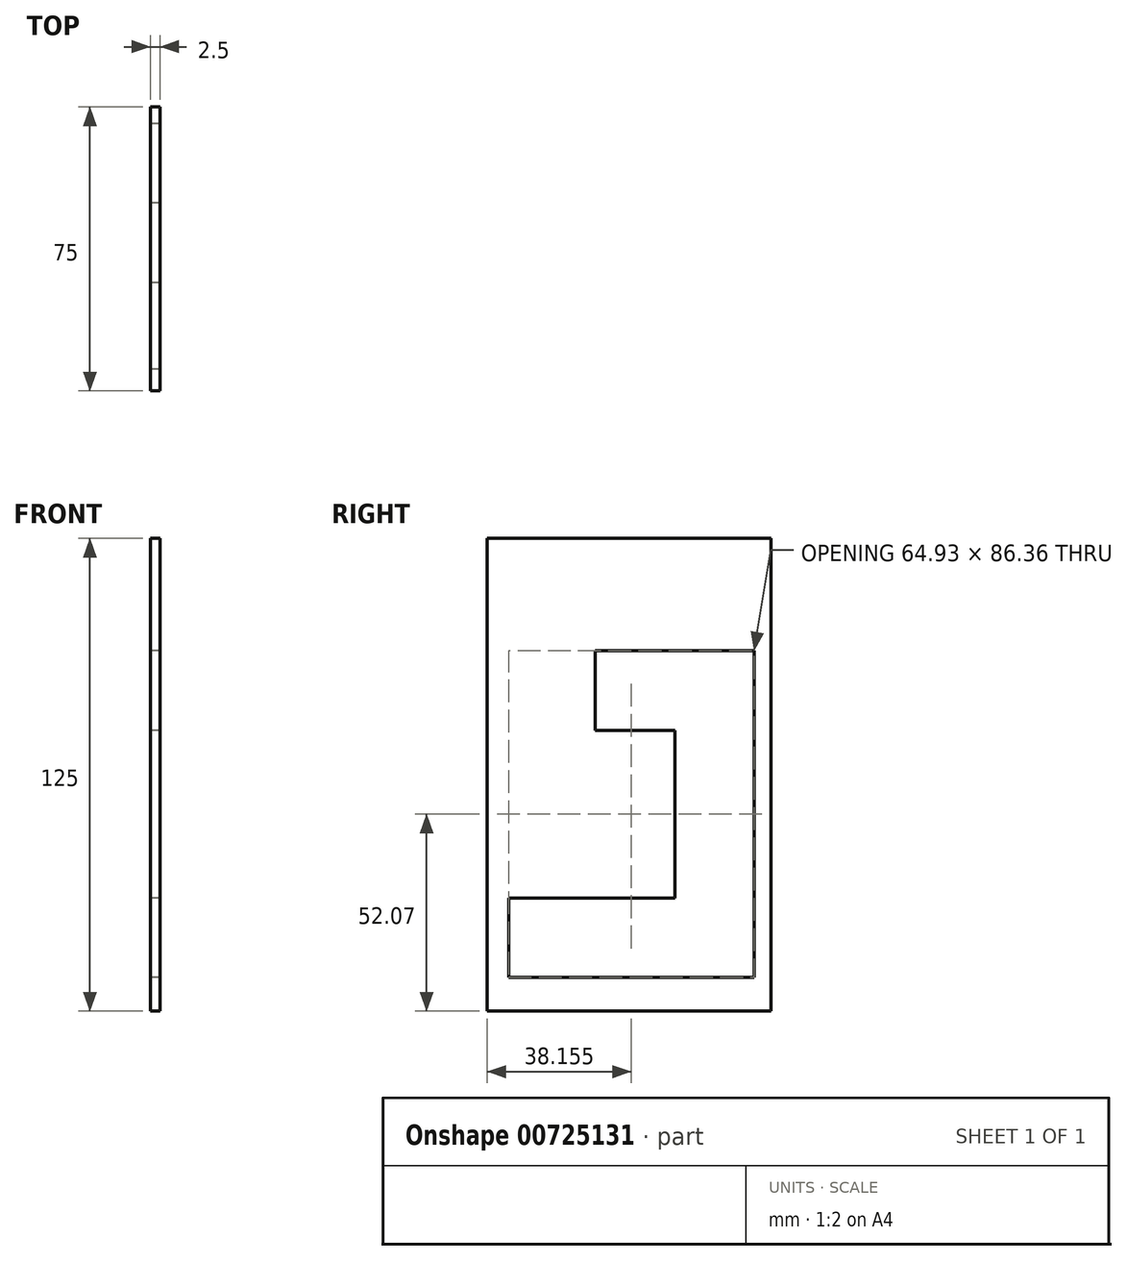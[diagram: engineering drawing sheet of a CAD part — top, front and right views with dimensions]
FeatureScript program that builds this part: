
annotation { "Feature Type Name" : "Feature", "Feature Type Description" : "" }
export const myFeature = defineFeature(function(context is Context, id is Id, definition is map)
    precondition{}
    {
        {
            var Q0;
            Q0=qCreatedBy(makeId("Right.planeOp"),FACE);
            var sketch = newSketch(context, id + "F0", { "sketchPlane" : qUnion([Q0])});
            skLineSegment(sketch, "E0.bottom", {"start": v(0, 0) * mm, "end": v(75, 0) * mm});
            skLineSegment(sketch, "E0.left", {"start": v(0, 0) * mm, "end": v(0, 125) * mm});
            skLineSegment(sketch, "E1.top", {"start": v(3.8, 3.81) * mm, "end": v(72.5, 3.81) * mm});
            skLineSegment(sketch, "E1.left", {"start": v(3.8, 121.19) * mm, "end": v(3.8, 3.8) * mm});
            skLineSegment(sketch, "E2.top", {"start": v(0, 125) * mm, "end": v(44.5, 125) * mm});
            skLineSegment(sketch, "E3", {"start": v(3.8, 121.19) * mm, "end": v(44.5, 121.19) * mm});
            skLineSegment(sketch, "E4", {"start": v(72.5, 3.81) * mm, "end": v(72.5, 125) * mm});
            skLineSegment(sketch, "E5", {"start": v(72.5, 125) * mm, "end": v(75, 125) * mm});
            skLineSegment(sketch, "E6", {"start": v(75, 125) * mm, "end": v(75, 0) * mm});
            skLineSegment(sketch, "E7", {"start": v(44.5, 121.19) * mm, "end": v(72.5, 121.19) * mm});
            skLineSegment(sketch, "E8", {"start": v(72.5, 121.2) * mm, "end": v(72.5, 125) * mm});
            skLineSegment(sketch, "E9", {"start": v(44.5, 125) * mm, "end": v(72.5, 125) * mm});
            skLineSegment(sketch, "E10", {"start": v(5.7, 29.9) * mm, "end": v(49.62, 29.9) * mm});
            skLineSegment(sketch, "E11", {"start": v(49.62, 29.9) * mm, "end": v(49.62, 74.25) * mm});
            skLineSegment(sketch, "E12", {"start": v(49.62, 74.25) * mm, "end": v(28.62, 74.25) * mm});
            skLineSegment(sketch, "E13", {"start": v(28.62, 74.25) * mm, "end": v(28.62, 95.25) * mm});
            skLineSegment(sketch, "E14", {"start": v(28.62, 95.25) * mm, "end": v(70.62, 95.25) * mm});
            skLineSegment(sketch, "E15", {"start": v(70.62, 95.25) * mm, "end": v(70.62, 8.9) * mm});
            skLineSegment(sketch, "E16", {"start": v(70.62, 8.9) * mm, "end": v(5.7, 8.89) * mm});
            skLineSegment(sketch, "E17", {"start": v(5.7, 8.89) * mm, "end": v(5.7, 29.9) * mm});
            skSolve(sketch);
        }
        {
            var Q0;
            Q0=makeQuery(id+"F0.imprint","IMPRINT",FACE,{"disambiguationData":[TD([[makeQuery(id+"F0.imprint","IMPRINT",EDGE,{"derivedFrom":sQuery(id+"F0.wireOp",EDGE,"E0.bottom")}),1.0]])]});
            var Q1;
            {var subQ1=sQuery(id+"F0.wireOp",EDGE,"E1.top");Q1=makeQuery(id+"F0.imprint","IMPRINT",FACE,{"disambiguationData":[TD([[makeQuery(id+"F0.imprint","IMPRINT",EDGE,{"derivedFrom":subQ1}),1.0]])]});}
            extrude(context, id + "F1", {"entities" : qUnion([Q0, Q1]), "depth" : 2.5 * mm, "offsetDistance" : 25.4 * mm});
        }
    });
